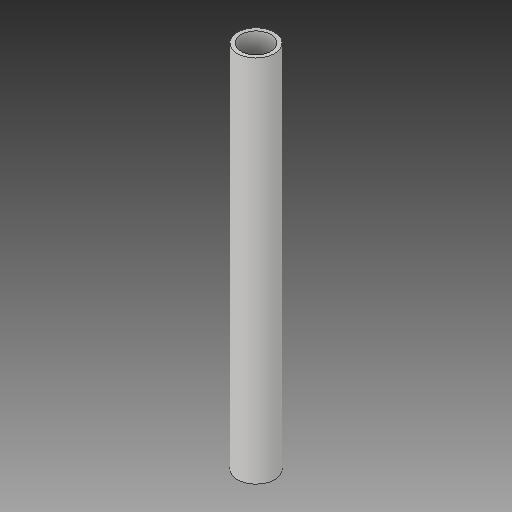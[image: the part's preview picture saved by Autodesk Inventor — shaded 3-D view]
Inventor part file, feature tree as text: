
AUTODESK INVENTOR PART (.ipt)
format: ipt  version: 2019.2 (Build 232265000, 265)  size: 98,304 bytes
history: native  units: mm
features: other x4, plane x1, extrude x1, sketch x1, reference x1
ambient origin geometry x8: Origin, YZ Plane, XZ Plane, XY Plane, X Axis, Y Axis, Z Axis, Center Point
bodies: Body1 (feature_tree)
feature tree (8):
  plane  "Work Plane2"
  extrude  "Extrusion2"  Depth=158.0mm
  sketch  "Sketch2"  dims[d4=15.875mm d5=1.6mm d6=158.0mm d7=0.0mm]
  reference  "Reference2"
  other  "<userpath>\Desktop\3dprojects\OpenEmoto\Hub\Hub.iam"
  other  "Hub.iam"
  other  "Bearing:2"
  other  "DIN 628 SKF - 7..B SKF 7200 BECBP:1"
